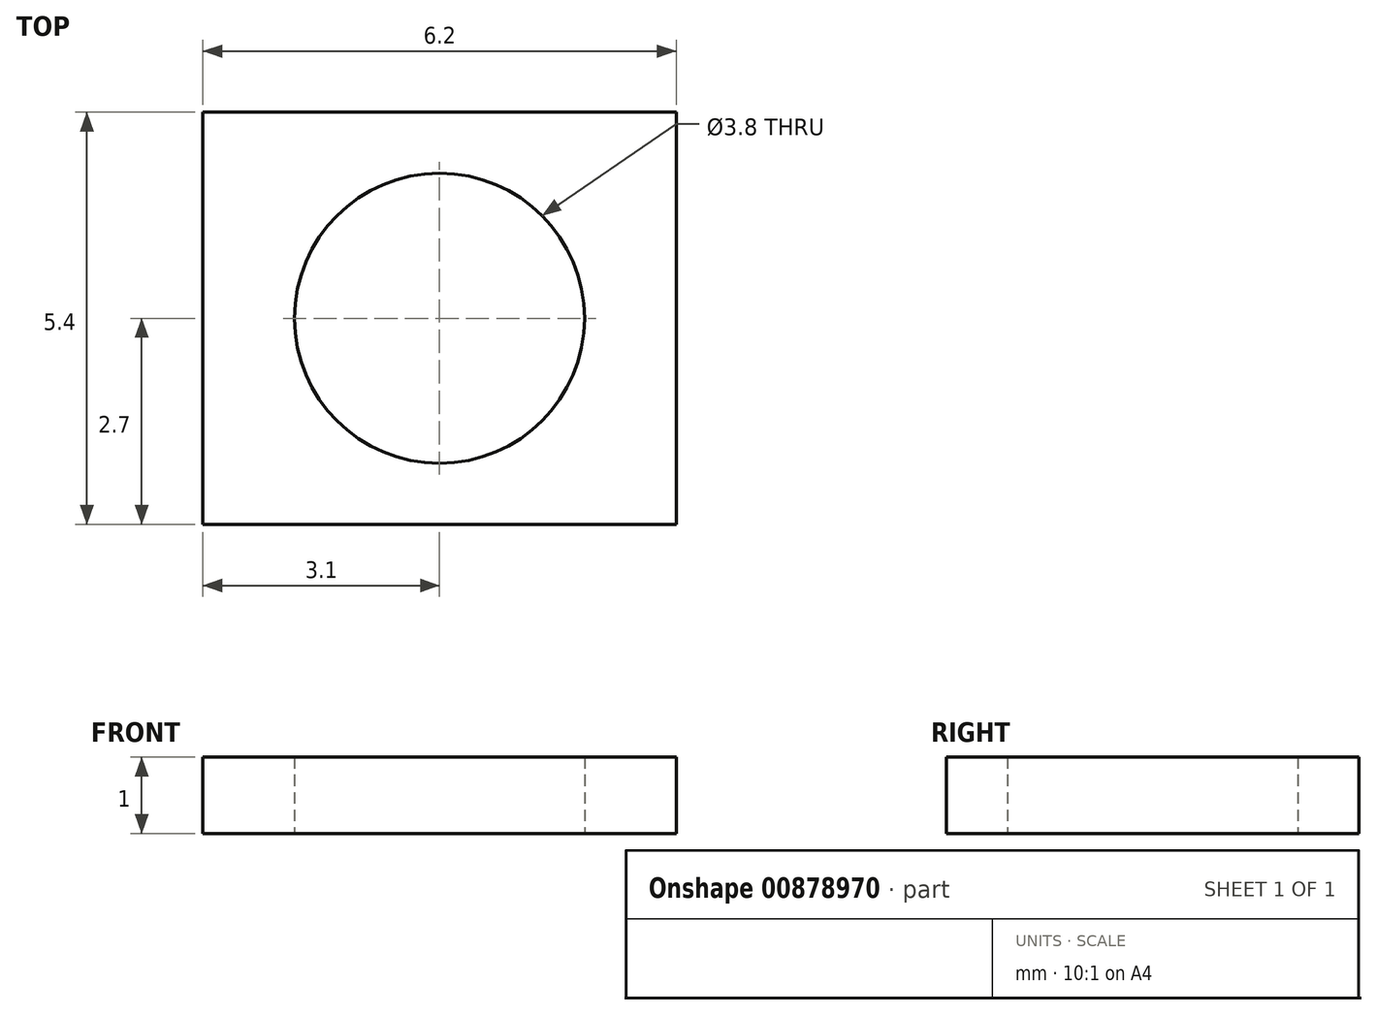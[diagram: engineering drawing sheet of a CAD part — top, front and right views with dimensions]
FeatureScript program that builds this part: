
annotation { "Feature Type Name" : "Feature", "Feature Type Description" : "" }
export const myFeature = defineFeature(function(context is Context, id is Id, definition is map)
    precondition{}
    {
        {
            var Q0;
            Q0=qCreatedBy(makeId("Top.planeOp"),FACE);
            var sketch = newSketch(context, id + "F0", { "sketchPlane" : qUnion([Q0])});
            skLineSegment(sketch, "E0.bottom", {"start": v(-3.1, 2.7) * mm, "end": v(3.1, 2.7) * mm});
            skLineSegment(sketch, "E0.top", {"start": v(-3.1, -2.7) * mm, "end": v(3.1, -2.7) * mm});
            skLineSegment(sketch, "E0.left", {"start": v(-3.1, 2.7) * mm, "end": v(-3.1, -2.7) * mm});
            skLineSegment(sketch, "E0.right", {"start": v(3.1, 2.7) * mm, "end": v(3.1, -2.7) * mm});
            skPoint(sketch, "E0.middle", {"position": v(0, 0) * mm});
            skCircle(sketch, "E1", {"center": v(0, 0) * mm, "radius": 1.9 * mm});
            skSolve(sketch);
        }
        {
            var Q0;
            Q0 = qSketchRegion(id + "F0", true);
            extrude(context, id + "F1", {"entities" : qUnion([Q0]), "depth" : 1 * mm, "offsetDistance" : 25 * mm});
        }
    });
